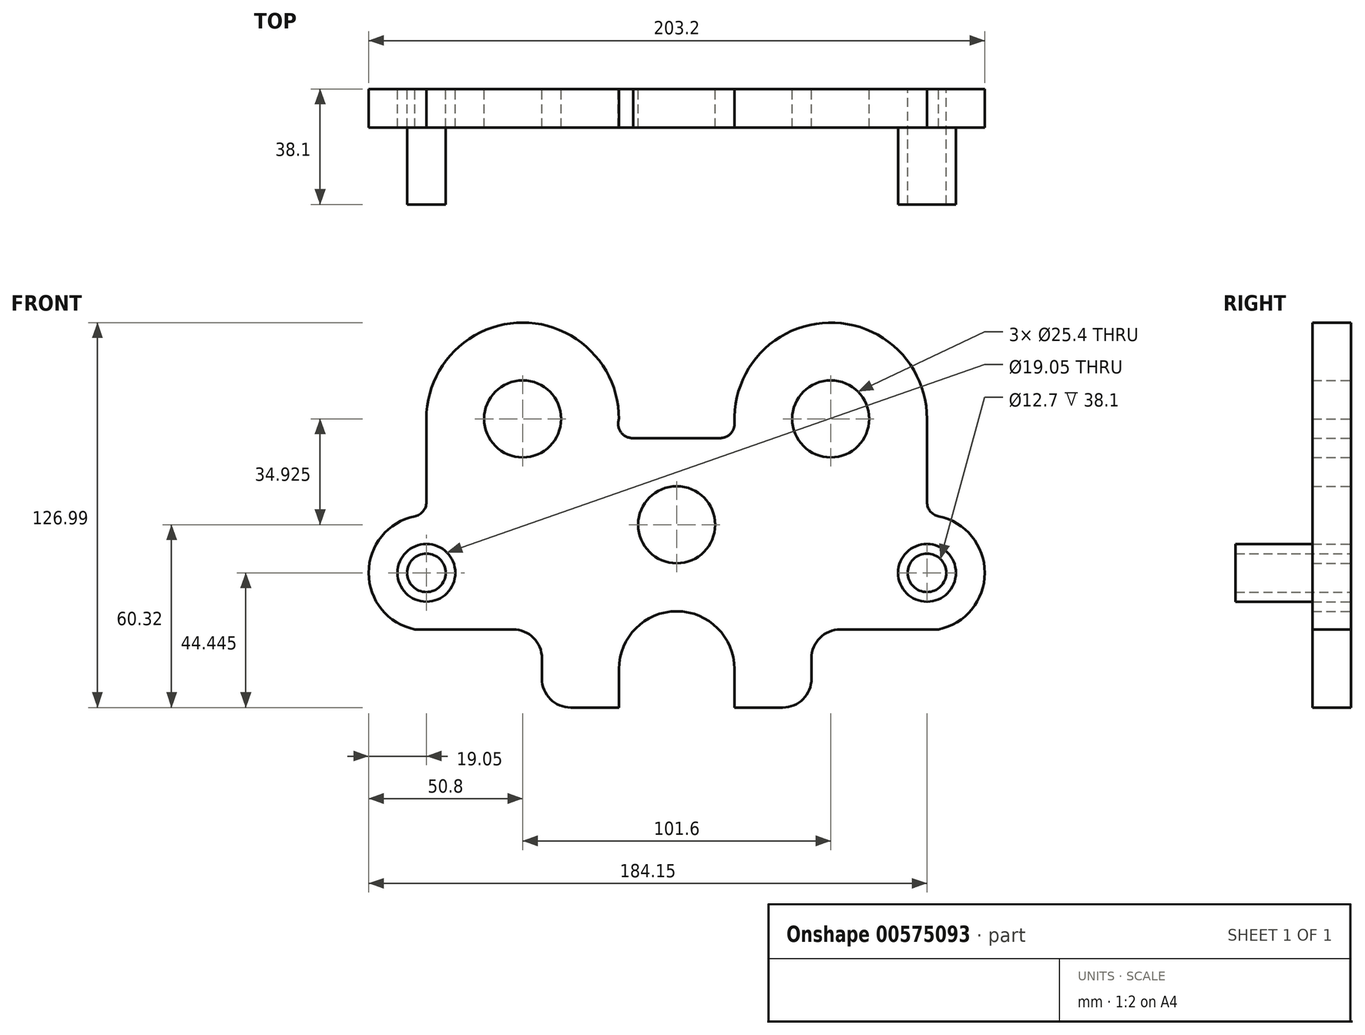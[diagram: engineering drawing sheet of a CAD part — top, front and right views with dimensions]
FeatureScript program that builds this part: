
annotation { "Feature Type Name" : "Feature", "Feature Type Description" : "" }
export const myFeature = defineFeature(function(context is Context, id is Id, definition is map)
    precondition{}
    {
        {
            var Q0;
            Q0=qCreatedBy(makeId("Front.planeOp"),FACE);
            var sketch = newSketch(context, id + "F0", { "sketchPlane" : qUnion([Q0])});
            skCircle(sketch, "E0", {"center": v(0, 0) * mm, "radius": 12.7 * mm});
            skArc(sketch, "E1.filletArc", {"start": v(14.37, 28.58) * mm, "mid": v(17.78, 30.06) * mm, "end": v(19.08, 33.54) * mm});
            skArc(sketch, "E2", {"start": v(19.08, 33.54) * mm, "mid": v(50.1, 66.67) * mm, "end": v(82.55, 34.93) * mm});
            skArc(sketch, "E3", {"start": v(86.36, -34.54) * mm, "mid": v(101.6, -15.88) * mm, "end": v(86.36, 2.8) * mm});
            skLineSegment(sketch, "E4", {"start": v(57.16, 34.12) * mm, "end": v(57.16, 34.12) * mm});
            skPoint(sketch, "E5", {"position": v(50.8, 66.67) * mm});
            skPoint(sketch, "E6", {"position": v(101.6, -15.88) * mm});
            skCircle(sketch, "E7", {"center": v(82.55, -15.88) * mm, "radius": 6.35 * mm});
            skArc(sketch, "E8.MirrorCS", {"start": v(-14.37, 28.58) * mm, "mid": v(-18.36, 30.49) * mm, "end": v(-19.05, 34.86) * mm});
            skArc(sketch, "E9.MirrorCS", {"start": v(-19.05, 34.86) * mm, "mid": v(-50.77, 66.67) * mm, "end": v(-82.55, 34.92) * mm});
            skArc(sketch, "E10.MirrorCS", {"start": v(-86.36, -34.54) * mm, "mid": v(-101.6, -15.88) * mm, "end": v(-86.36, 2.8) * mm});
            skCircle(sketch, "E11.MirrorC", {"center": v(-82.55, -15.88) * mm, "radius": 6.35 * mm});
            skCircle(sketch, "E12", {"center": v(50.8, 34.93) * mm, "radius": 12.7 * mm});
            skCircle(sketch, "E13", {"center": v(-50.8, 34.92) * mm, "radius": 12.7 * mm});
            skLineSegment(sketch, "E14", {"start": v(-14.37, 28.58) * mm, "end": v(14.37, 28.58) * mm});
            skPoint(sketch, "E15", {"position": v(-101.6, -15.88) * mm});
            skPoint(sketch, "E16", {"position": v(-50.83, 66.67) * mm});
            skPoint(sketch, "E16.positionSnap0", {"position": v(-50.77, 66.67) * mm});
            skLineSegment(sketch, "E17", {"start": v(-19.05, -60.33) * mm, "end": v(-19.05, -47.63) * mm});
            skLineSegment(sketch, "E18", {"start": v(19.05, -47.63) * mm, "end": v(19.05, -60.33) * mm});
            skArc(sketch, "E19", {"start": v(-19.05, -47.63) * mm, "mid": v(-13.47, -34.15) * mm, "end": v(0, -28.58) * mm});
            skArc(sketch, "E20", {"start": v(19.05, -47.63) * mm, "mid": v(13.47, -34.15) * mm, "end": v(0, -28.58) * mm});
            skLineSegment(sketch, "E21", {"start": v(19.05, -60.33) * mm, "end": v(34.93, -60.33) * mm});
            skLineSegment(sketch, "E22", {"start": v(-19.05, -60.33) * mm, "end": v(-34.92, -60.33) * mm});
            skLineSegment(sketch, "E23", {"start": v(-44.45, -50.8) * mm, "end": v(-44.45, -44.07) * mm});
            skLineSegment(sketch, "E24", {"start": v(44.45, -50.8) * mm, "end": v(44.45, -44.07) * mm});
            skLineSegment(sketch, "E25", {"start": v(53.98, -34.54) * mm, "end": v(86.36, -34.54) * mm});
            skLineSegment(sketch, "E26", {"start": v(-53.97, -34.54) * mm, "end": v(-86.36, -34.54) * mm});
            skPoint(sketch, "E27.visualSharp", {"position": v(-44.45, -60.33) * mm});
            skArc(sketch, "E27.filletArc", {"start": v(-44.45, -50.8) * mm, "mid": v(-41.66, -57.54) * mm, "end": v(-34.92, -60.33) * mm});
            skPoint(sketch, "E28.visualSharp", {"position": v(-44.45, -34.54) * mm});
            skArc(sketch, "E28.filletArc", {"start": v(-44.45, -44.07) * mm, "mid": v(-47.24, -37.33) * mm, "end": v(-53.97, -34.54) * mm});
            skPoint(sketch, "E29.visualSharp", {"position": v(44.45, -34.54) * mm});
            skArc(sketch, "E29.filletArc", {"start": v(53.98, -34.54) * mm, "mid": v(47.24, -37.33) * mm, "end": v(44.45, -44.07) * mm});
            skPoint(sketch, "E30.visualSharp", {"position": v(44.45, -60.33) * mm});
            skArc(sketch, "E30.filletArc", {"start": v(34.93, -60.32) * mm, "mid": v(41.66, -57.54) * mm, "end": v(44.45, -50.8) * mm});
            skLineSegment(sketch, "E31", {"start": v(82.55, 34.93) * mm, "end": v(82.55, 7.46) * mm});
            skLineSegment(sketch, "E32", {"start": v(-82.55, 7.46) * mm, "end": v(-82.55, 34.92) * mm});
            skArc(sketch, "E33.filletArc", {"start": v(-86.36, 2.8) * mm, "mid": v(-83.62, 4.44) * mm, "end": v(-82.55, 7.46) * mm});
            skArc(sketch, "E34.filletArc", {"start": v(82.55, 7.46) * mm, "mid": v(83.62, 4.44) * mm, "end": v(86.36, 2.8) * mm});
            skCircle(sketch, "E35.0", {"center": v(-82.55, -15.88) * mm, "radius": 9.52 * mm});
            skCircle(sketch, "E36.0", {"center": v(82.55, -15.88) * mm, "radius": 9.53 * mm});
            skSolve(sketch);
        }
        {
            var Q0;
            Q0=makeQuery(id+"F0.imprint","IMPRINT",FACE,{"disambiguationData":[TD([[makeQuery(id+"F0.imprint","IMPRINT",EDGE,{"derivedFrom":sQuery(id+"F0.wireOp",EDGE,"E0")}),-1.0]])]});
            extrude(context, id + "F1", {"entities" : qUnion([Q0]), "depth" : 12.7 * mm, "offsetDistance" : 25.4 * mm});
        }
        {
            var Q0;
            Q0=makeQuery(id+"F0.imprint","IMPRINT",FACE,{"disambiguationData":[TD([[makeQuery(id+"F0.imprint","IMPRINT",EDGE,{"derivedFrom":sQuery(id+"F0.wireOp",EDGE,"E11.MirrorC")}),1.0]])]});
            var Q1;
            Q1=makeQuery(id+"F0.imprint","IMPRINT",FACE,{"disambiguationData":[TD([[makeQuery(id+"F0.imprint","IMPRINT",EDGE,{"derivedFrom":sQuery(id+"F0.wireOp",EDGE,"E7")}),-1.0]])]});
            extrude(context, id + "F2", {"entities" : qUnion([Q0, Q1]), "operationType" : NewBodyOperationType.ADD, "depth" : 38.1 * mm, "offsetDistance" : 25.4 * mm});
        }
    });
